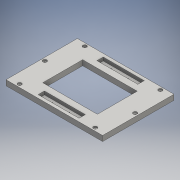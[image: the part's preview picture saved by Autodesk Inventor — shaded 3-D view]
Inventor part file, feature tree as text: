
AUTODESK INVENTOR PART (.ipt)
format: ipt  version: 2016 (Build 200138000, 138)  size: 163,328 bytes
history: native  units: mm
features: sketch x4, mirror x3, extrude x2, hole x2
ambient origin geometry x8: Origin, YZ Plane, XZ Plane, XY Plane, X Axis, Y Axis, Z Axis, Center Point
bodies: Solid1 (feature_tree)
feature tree (11):
  extrude  "Extrusion1"  Depth=340.0mm
  extrude  "Extrusion2"  Depth=230.0mm
  hole  "Hole1"  [1 undecoded]
  mirror  "Mirror2"
  hole  "Hole2"  [1 undecoded]
  mirror  "Mirror3"
  mirror  "Mirror4"
  sketch  "Sketch1"  dims[d0=460.0mm d1=340.0mm]
  sketch  "Sketch2"  dims[d2=170.0mm d3=230.0mm]
  sketch  "Sketch3"  dims[d4=100.0mm d5=100.0mm]
  sketch  "Sketch4"  dims[d6=75.0mm d7=75.0mm d8=25.0mm d9=0.0mm d10=30.0mm d11=195.0mm d12=15.0mm d13=16.0mm d14=0.0mm d15=15.0mm d16=80.0mm d17=40.0mm d18=5.5mm d19=6.0mm d20=4.0mm d21=2.0mm d22=90.0deg d23=8.0mm d24=20.594885mm d25=15.0mm d26=15.0mm d27=50.0mm d28=6.6mm d29=6.0mm d30=18.0mm d31=6.6mm d32=90.0deg d33=8.0mm d34=20.594885mm]
note: 2 required parameter values undecoded (feature->parameter linkage not recoverable at this tier; creation-order binding heuristic only, values carry confidence <= 0.55)
